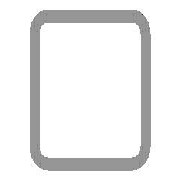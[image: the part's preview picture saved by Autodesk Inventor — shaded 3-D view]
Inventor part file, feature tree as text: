
AUTODESK INVENTOR PART (.ipt)
format: ipt  version: 2025.3 (Build 293356000, 356)  size: 133,632 bytes
history: native  units: mm (DEFAULTED — no unit token found)
features: other x4, sketch x1, plane x1
ambient origin geometry x8: Origin, YZ Plane, XZ Plane, XY Plane, X Axis, Y Axis, Z Axis, Center Point
bodies: Solid1 (feature_tree), Body (feature_tree)
feature tree (6):
  parser-record x1  (decoder bookkeeping rows leaked as tree rows — omitted from the tree; the rows remain in map.json)
  other  "Driven Length"
  other  "Start Plane"
  other  "End Plane"
  sketch  "Sketch3"  dims[d3=2040.0mm d4=0.0mm d7=4.0mm d9=40.0mm d11=40.0mm d12=2.0mm d13=80.0mm d14=2120.0mm d15=20.0mm d16=20.0mm d17=90.0deg d18=2040.0mm]
  plane  "Work Plane3"
